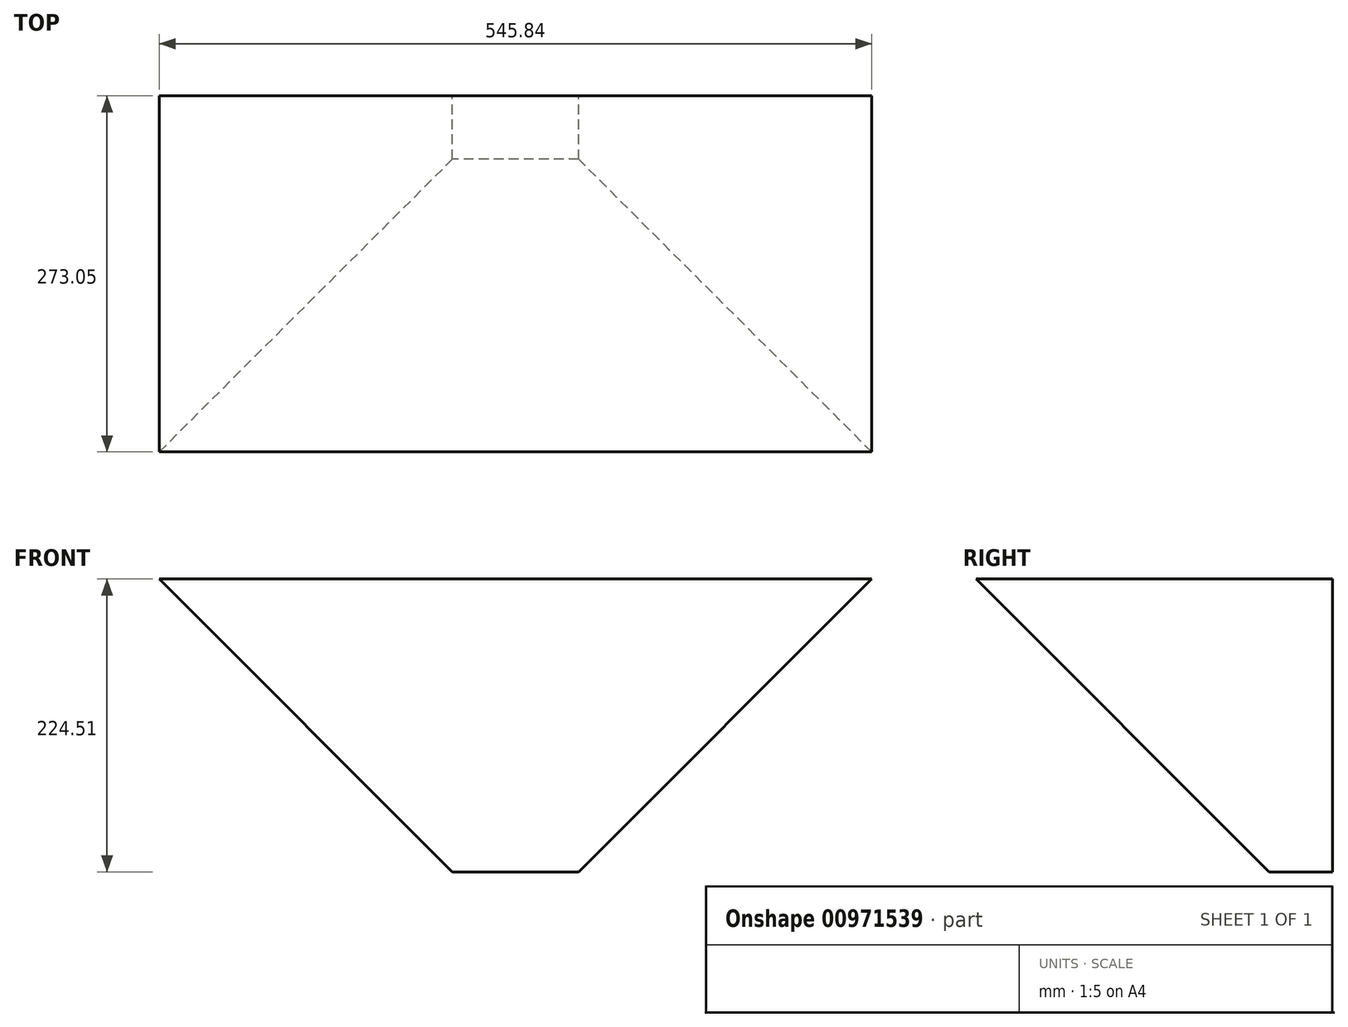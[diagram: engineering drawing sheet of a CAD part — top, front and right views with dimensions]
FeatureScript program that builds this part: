
annotation { "Feature Type Name" : "Feature", "Feature Type Description" : "" }
export const myFeature = defineFeature(function(context is Context, id is Id, definition is map)
    precondition{}
    {
        {
            var Q0;
            Q0=qCreatedBy(makeId("Top.planeOp"),FACE);
            var sketch = newSketch(context, id + "F0", { "sketchPlane" : qUnion([Q0])});
            skLineSegment(sketch, "E0.bottom", {"start": v(-254.12, 152.41) * mm, "end": v(291.72, 152.41) * mm});
            skLineSegment(sketch, "E0.top", {"start": v(-254.12, -120.64) * mm, "end": v(291.72, -120.64) * mm});
            skLineSegment(sketch, "E0.left", {"start": v(-254.12, 152.41) * mm, "end": v(-254.12, -120.64) * mm});
            skLineSegment(sketch, "E0.right", {"start": v(291.72, 152.41) * mm, "end": v(291.72, -120.64) * mm});
            skSolve(sketch);
        }
        {
            var Q0;
            Q0=makeQuery(id+"F0.imprint","IMPRINT",FACE,{"disambiguationData":[TD([[makeQuery(id+"F0.imprint","IMPRINT",EDGE,{"derivedFrom":sQuery(id+"F0.wireOp",EDGE,"E0.bottom")}),-1.0]])]});
            extrude(context, id + "F1", {"entities" : qUnion([Q0]), "depth" : 317.5 * mm, "offsetDistance" : 25.4 * mm});
        }
        {
            var Q0;
            Q0=makeQuery(id+"F1.opExtrude","SWEPT_FACE",FACE,{"disambiguationData":[OSD([sQuery(id+"F0.wireOp",EDGE,"E0.bottom")])]});
            var sketch = newSketch(context, id + "F2", { "sketchPlane" : qUnion([Q0])});
            skLineSegment(sketch, "E1", {"start": v(25.78, 0) * mm, "end": v(-63.38, 0) * mm});
            skLineSegment(sketch, "E2", {"start": v(-291.72, 317.5) * mm, "end": v(254.12, 317.5) * mm});
            skLineSegment(sketch, "E3", {"start": v(254.12, 317.5) * mm, "end": v(-291.72, 317.5) * mm});
            skLineSegment(sketch, "E4", {"start": v(29.61, 92.99) * mm, "end": v(254.12, 317.5) * mm});
            skLineSegment(sketch, "E5", {"start": v(-67.21, 92.99) * mm, "end": v(-291.72, 317.5) * mm});
            skLineSegment(sketch, "E6", {"start": v(29.61, 92.99) * mm, "end": v(-67.21, 92.99) * mm});
            skSolve(sketch);
        }
        {
            var Q0;
            Q0=makeQuery(id+"F1.opExtrude","SWEPT_FACE",FACE,{"disambiguationData":[OSD([sQuery(id+"F0.wireOp",EDGE,"E0.left")])]});
            var sketch = newSketch(context, id + "F3", { "sketchPlane" : qUnion([Q0])});
            skLineSegment(sketch, "E7", {"start": v(-152.41, 92.99) * mm, "end": v(-103.86, 92.99) * mm});
            skLineSegment(sketch, "E8", {"start": v(-103.86, 92.99) * mm, "end": v(120.64, 317.5) * mm});
            skLineSegment(sketch, "E9", {"start": v(120.64, 317.5) * mm, "end": v(-152.41, 317.5) * mm});
            skLineSegment(sketch, "E10", {"start": v(-152.41, 317.5) * mm, "end": v(-152.41, 92.99) * mm});
            skSolve(sketch);
        }
        {
            var Q0;
            {var subQ3=sQuery(id+"F3.wireOp",EDGE,"E7");Q0=makeQuery(id+"F3.imprint","IMPRINT",FACE,{"disambiguationData":[TD([[makeQuery(id+"F3.imprint","IMPRINT",EDGE,{"derivedFrom":subQ3}),-1.0]])]});}
            extrude(context, id + "F4", {"entities" : qUnion([Q0]), "operationType" : NewBodyOperationType.REMOVE, "endBound" : BoundingType.THROUGH_ALL, "oppositeDirection" : true, "depth" : 25.4 * mm, "offsetDistance" : 25.4 * mm});
        }
        {
            var Q0;
            {var subQ0=sQuery(id+"F2.wireOp",EDGE,"E1");Q0=makeQuery(id+"F2.imprint","IMPRINT",FACE,{"disambiguationData":[TD([[makeQuery(id+"F2.imprint","IMPRINT",EDGE,{"derivedFrom":subQ0}),-1.0]])]});}
            extrude(context, id + "F5", {"entities" : qUnion([Q0]), "operationType" : NewBodyOperationType.REMOVE, "endBound" : BoundingType.THROUGH_ALL, "oppositeDirection" : true, "depth" : 25.4 * mm, "offsetDistance" : 25.4 * mm});
        }
    });
